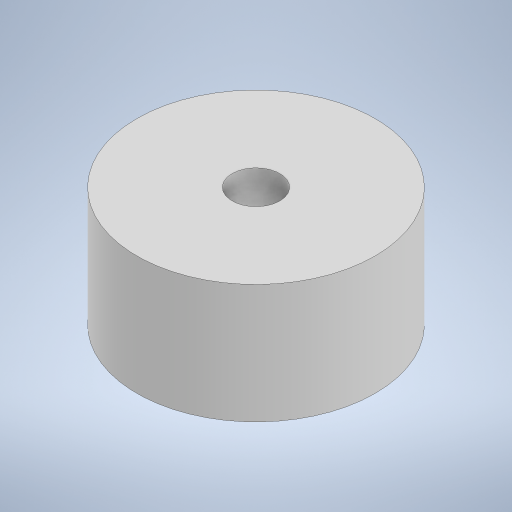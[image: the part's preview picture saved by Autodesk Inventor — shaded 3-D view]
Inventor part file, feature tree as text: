
AUTODESK INVENTOR PART (.ipt)
format: ipt  version: 2023 (Build 270158000, 158)  size: 200,704 bytes
history: native  units: mm
features: extrude x2, sketch x2, other x1
ambient origin geometry x8: Origin, YZ Plane, XZ Plane, XY Plane, X Axis, Y Axis, Z Axis, Center Point
bodies: Body1 (feature_tree)
feature tree (5):
  other  "Твердое тело1"
  extrude  "Выдавливание1"  Depth=20.0mm
  extrude  "Выдавливание2"  Depth=10.0mm TaperAngle=0.0deg
  sketch  "Эскиз1"
  sketch  "Эскиз2"
